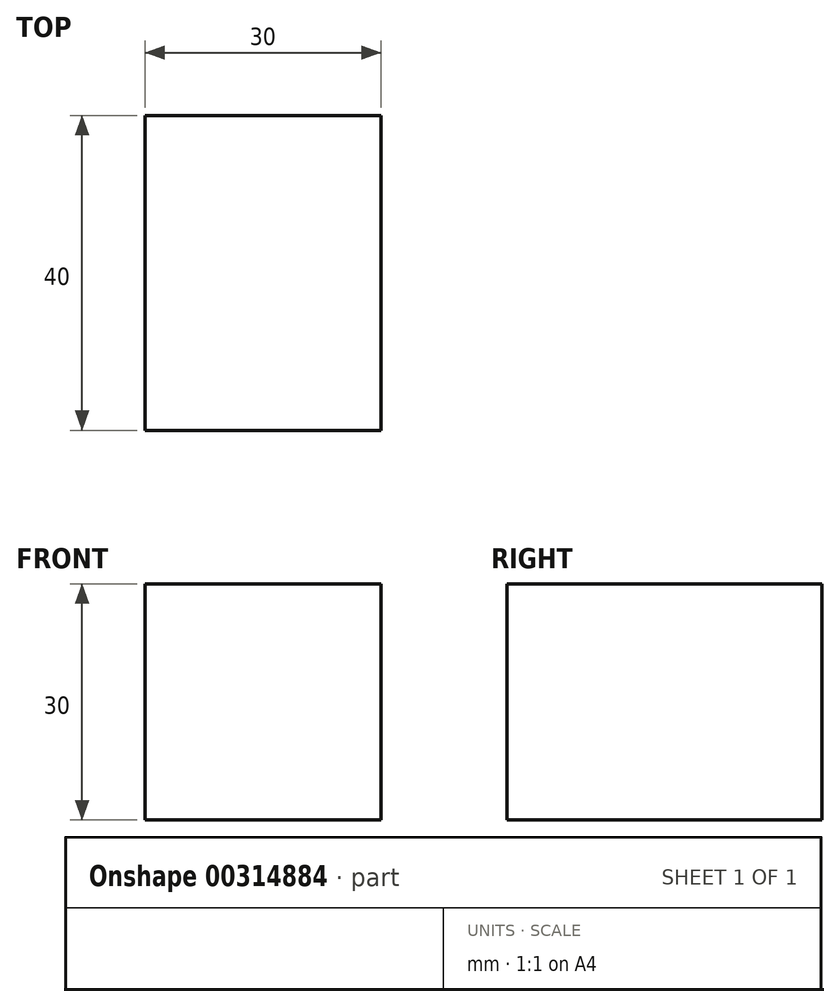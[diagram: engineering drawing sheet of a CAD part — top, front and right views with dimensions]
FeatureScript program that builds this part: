
annotation { "Feature Type Name" : "Feature", "Feature Type Description" : "" }
export const myFeature = defineFeature(function(context is Context, id is Id, definition is map)
    precondition{}
    {
        {
            var Q0;
            Q0=qCreatedBy(makeId("Front.planeOp"),FACE);
            var sketch = newSketch(context, id + "F0", { "sketchPlane" : qUnion([Q0])});
            skLineSegment(sketch, "E0.bottom", {"start": v(15, 15) * mm, "end": v(-15, 15) * mm});
            skLineSegment(sketch, "E0.top", {"start": v(15, -15) * mm, "end": v(-15, -15) * mm});
            skLineSegment(sketch, "E0.left", {"start": v(15, 15) * mm, "end": v(15, -15) * mm});
            skLineSegment(sketch, "E0.right", {"start": v(-15, 15) * mm, "end": v(-15, -15) * mm});
            skPoint(sketch, "E0.middle", {"position": v(0, 0) * mm});
            skLineSegment(sketch, "E1", {"start": v(-15, 0) * mm, "end": v(15, 0) * mm, "construction": true});
            skLineSegment(sketch, "E2", {"start": v(-15, 15) * mm, "end": v(15, 0) * mm, "construction": true});
            skLineSegment(sketch, "E3", {"start": v(15, 15) * mm, "end": v(-15, 0) * mm, "construction": true});
            skLineSegment(sketch, "E4", {"start": v(-15, 0) * mm, "end": v(15, -15) * mm, "construction": true});
            skLineSegment(sketch, "E5", {"start": v(15, 0) * mm, "end": v(-15, -15) * mm, "construction": true});
            skLineSegment(sketch, "E6.bottom", {"start": v(6, 10.5) * mm, "end": v(-6, 10.5) * mm});
            skLineSegment(sketch, "E6.top", {"start": v(6, 4.5) * mm, "end": v(-6, 4.5) * mm});
            skLineSegment(sketch, "E6.left", {"start": v(6, 10.5) * mm, "end": v(6, 4.5) * mm});
            skLineSegment(sketch, "E6.right", {"start": v(-6, 10.5) * mm, "end": v(-6, 4.5) * mm});
            skPoint(sketch, "E6.middle", {"position": v(0, 7.5) * mm});
            skLineSegment(sketch, "E7.bottom", {"start": v(6, -4.5) * mm, "end": v(-6, -4.5) * mm});
            skLineSegment(sketch, "E7.top", {"start": v(6, -10.5) * mm, "end": v(-6, -10.5) * mm});
            skLineSegment(sketch, "E7.left", {"start": v(6, -4.5) * mm, "end": v(6, -10.5) * mm});
            skLineSegment(sketch, "E7.right", {"start": v(-6, -4.5) * mm, "end": v(-6, -10.5) * mm});
            skPoint(sketch, "E7.middle", {"position": v(0, -7.5) * mm});
            skSolve(sketch);
        }
        {
            var Q0;
            Q0=makeQuery(id+"F0.imprint","IMPRINT",FACE,{"disambiguationData":[TD([[makeQuery(id+"F0.imprint","IMPRINT",EDGE,{"derivedFrom":sQuery(id+"F0.wireOp",EDGE,"E0.bottom")}),1.0]])]});
            var Q1;
            Q1=makeQuery(id+"F0.imprint","IMPRINT",FACE,{"disambiguationData":[TD([[makeQuery(id+"F0.imprint","IMPRINT",EDGE,{"derivedFrom":sQuery(id+"F0.wireOp",EDGE,"E6.bottom")}),1.0]])]});
            var Q2;
            Q2=makeQuery(id+"F0.imprint","IMPRINT",FACE,{"disambiguationData":[TD([[makeQuery(id+"F0.imprint","IMPRINT",EDGE,{"derivedFrom":sQuery(id+"F0.wireOp",EDGE,"E7.bottom")}),1.0]])]});
            extrude(context, id + "F1", {"entities" : qUnion([Q0, Q1, Q2]), "depth" : 40 * mm});
        }
    });
